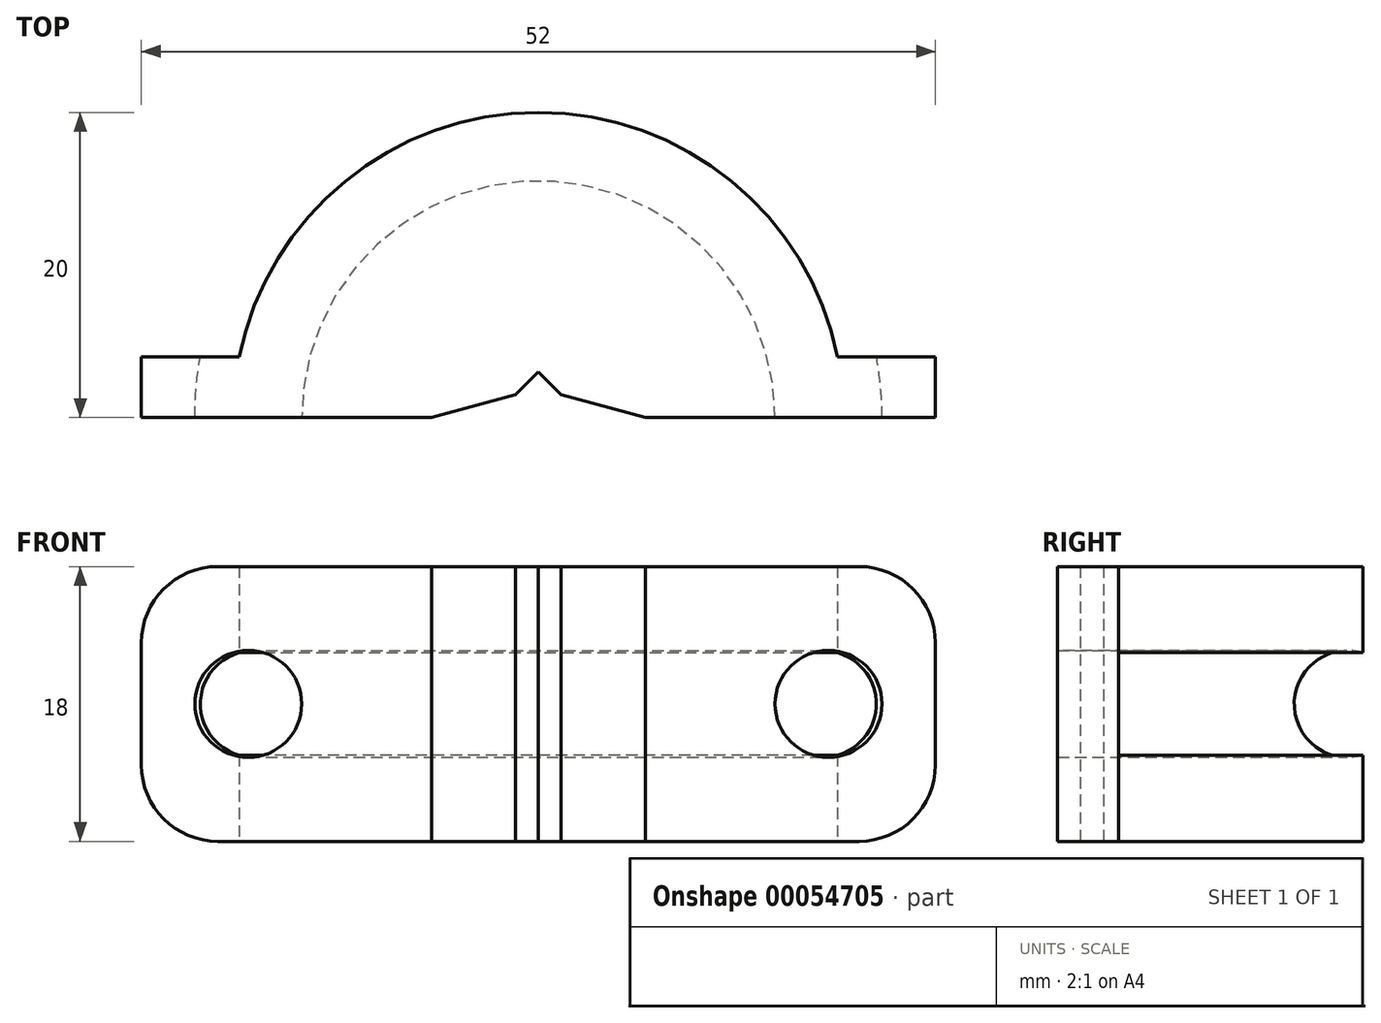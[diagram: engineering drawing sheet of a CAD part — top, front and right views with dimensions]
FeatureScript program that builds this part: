
annotation { "Feature Type Name" : "Feature", "Feature Type Description" : "" }
export const myFeature = defineFeature(function(context is Context, id is Id, definition is map)
    precondition{}
    {
        {
            var Q0;
            Q0=qCreatedBy(makeId("Top.planeOp"),FACE);
            var sketch = newSketch(context, id + "F0", { "sketchPlane" : qUnion([Q0])});
            skArc(sketch, "E0", {"start": v(19.6, 4) * mm, "mid": v(0, 20) * mm, "end": v(-19.6, 4) * mm});
            skLineSegment(sketch, "E1.bottom", {"start": v(-26, 0) * mm, "end": v(-7, 0) * mm});
            skLineSegment(sketch, "E1.top", {"start": v(-26, 4) * mm, "end": v(-19.6, 4) * mm});
            skLineSegment(sketch, "E1.left", {"start": v(-26, 0) * mm, "end": v(-26, 4) * mm});
            skLineSegment(sketch, "E1.right", {"start": v(26, 0) * mm, "end": v(26, 4) * mm});
            skLineSegment(sketch, "E2.trimOffspring", {"start": v(19.6, 4) * mm, "end": v(26, 4) * mm});
            skLineSegment(sketch, "E3", {"start": v(1.5, 1.5) * mm, "end": v(7, 0) * mm});
            skLineSegment(sketch, "E4", {"start": v(-1.5, 1.5) * mm, "end": v(-7, 0) * mm});
            skLineSegment(sketch, "E5", {"start": v(-1.5, 1.5) * mm, "end": v(0, 3) * mm});
            skLineSegment(sketch, "E6", {"start": v(0, 3) * mm, "end": v(1.5, 1.5) * mm});
            skLineSegment(sketch, "E7.trimOffspring", {"start": v(7, 0) * mm, "end": v(26, 0) * mm});
            skSolve(sketch);
        }
        {
            var Q0;
            Q0 = qSketchRegion(id + "F0", true);
            extrude(context, id + "F1", {"entities" : qUnion([Q0]), "depth" : 18 * mm});
        }
        {
            var Q0;
            Q0=makeQuery(id+"F1.opExtrude","SWEPT_FACE",FACE,{"disambiguationData":[OSD([sQuery(id+"F0.wireOp",EDGE,"E7.trimOffspring")])]});
            var sketch = newSketch(context, id + "F2", { "sketchPlane" : qUnion([Q0])});
            skCircle(sketch, "E8", {"center": v(19, 9) * mm, "radius": 3.5 * mm});
            skLineSegment(sketch, "E9", {"start": v(0, 22.28) * mm, "end": v(0, -10) * mm});
            skSolve(sketch);
        }
        {
            var Q0;
            Q0=makeQuery(id+"F2.imprint","IMPRINT",FACE,{"disambiguationData":[TD([[makeQuery(id+"F2.imprint","IMPRINT",EDGE,{"derivedFrom":sQuery(id+"F2.wireOp",EDGE,"E8")}),1.0]])]});
            var Q1;
            Q1=sQuery(id+"F2.wireOp",EDGE,"E9");
            revolve(context, id + "F3", {"operationType" : NewBodyOperationType.REMOVE, "entities" : qUnion([Q0]), "axis" : qUnion([Q1]), "revolveType" : RevolveType.FULL, "oppositeDirection" : true});
        }
        {
            var Q0;
            Q0=makeQuery(id+"F1.opExtrude","CAP_EDGE",EDGE,{"disambiguationData":[OSD([sQuery(id+"F0.wireOp",EDGE,"E1.right")])],"isStart":false});
            var Q1;
            Q1=makeQuery(id+"F1.opExtrude","CAP_EDGE",EDGE,{"disambiguationData":[OSD([sQuery(id+"F0.wireOp",EDGE,"E1.right")])],"isStart":true});
            var Q2;
            Q2=makeQuery(id+"F1.opExtrude","CAP_EDGE",EDGE,{"disambiguationData":[OSD([sQuery(id+"F0.wireOp",EDGE,"E1.left")])],"isStart":true});
            var Q3;
            Q3=makeQuery(id+"F1.opExtrude","CAP_EDGE",EDGE,{"disambiguationData":[OSD([sQuery(id+"F0.wireOp",EDGE,"E1.left")])],"isStart":false});
            fillet(context, id + "F4", {"entities" : qUnion([Q0, Q1, Q2, Q3]), "radius" : 5 * mm, "tangentPropagation" : true, "allowEdgeOverflow" : false});
        }
    });
